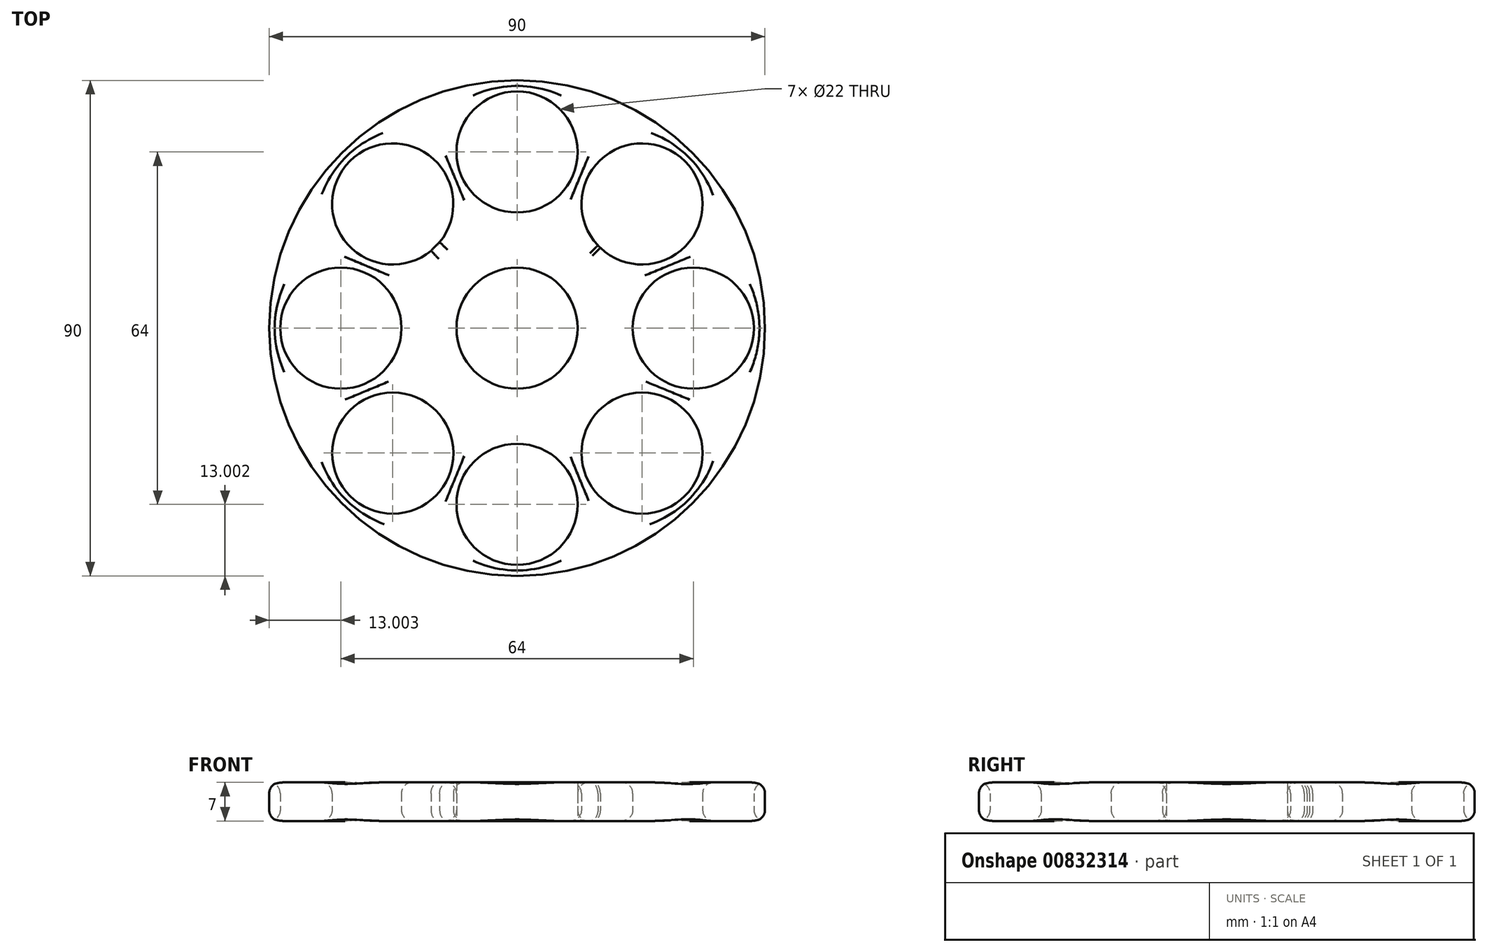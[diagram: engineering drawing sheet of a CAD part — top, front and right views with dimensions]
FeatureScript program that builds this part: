
annotation { "Feature Type Name" : "Feature", "Feature Type Description" : "" }
export const myFeature = defineFeature(function(context is Context, id is Id, definition is map)
    precondition{}
    {
        {
            var Q0;
            Q0=qCreatedBy(makeId("Top.planeOp"),FACE);
            var sketch = newSketch(context, id + "F0", { "sketchPlane" : qUnion([Q0])});
            skCircle(sketch, "E0", {"center": v(-30.12, 6.5) * mm, "radius": 11 * mm});
            skCircle(sketch, "E1", {"center": v(-62.12, 6.5) * mm, "radius": 11 * mm});
            skCircle(sketch, "E2", {"center": v(1.88, 6.5) * mm, "radius": 11 * mm});
            skCircle(sketch, "E3", {"center": v(-30.12, 38.5) * mm, "radius": 11 * mm});
            skCircle(sketch, "E4", {"center": v(-30.12, -25.5) * mm, "radius": 11 * mm});
            skCircle(sketch, "E5", {"center": v(-52.7, -16.2) * mm, "radius": 11 * mm});
            skCircle(sketch, "E6", {"center": v(-7.44, 29.05) * mm, "radius": 11 * mm});
            skCircle(sketch, "E7", {"center": v(-52.7, 29.05) * mm, "radius": 11 * mm});
            skCircle(sketch, "E8", {"center": v(-7.44, -16.2) * mm, "radius": 11 * mm});
            skCircle(sketch, "E9.0", {"center": v(-30.12, 38.5) * mm, "radius": 12 * mm});
            skCircle(sketch, "E10.0", {"center": v(-7.44, 29.05) * mm, "radius": 12 * mm});
            skCircle(sketch, "E11.0", {"center": v(1.88, 6.5) * mm, "radius": 12 * mm});
            skCircle(sketch, "E12.0", {"center": v(-7.44, -16.2) * mm, "radius": 11.13 * mm});
            skCircle(sketch, "E13.0", {"center": v(-7.44, -16.2) * mm, "radius": 12.13 * mm});
            skCircle(sketch, "E14.0", {"center": v(-30.12, -25.5) * mm, "radius": 12 * mm});
            skCircle(sketch, "E15.0", {"center": v(-52.7, -16.2) * mm, "radius": 12 * mm});
            skCircle(sketch, "E16.0", {"center": v(-62.12, 6.5) * mm, "radius": 12 * mm});
            skCircle(sketch, "E17.0", {"center": v(-52.7, 29.05) * mm, "radius": 12 * mm});
            skCircle(sketch, "E18.0", {"center": v(-30.12, 6.5) * mm, "radius": 21 * mm});
            skCircle(sketch, "E19", {"center": v(-30.12, 6.5) * mm, "radius": 45 * mm});
            skSolve(sketch);
        }
        {
            var Q0;
            Q0=makeQuery(id+"F0.imprint","IMPRINT",FACE,{"disambiguationData":[TD([[makeQuery(id+"F0.imprint","IMPRINT",EDGE,{"derivedFrom":sQuery(id+"F0.wireOp",EDGE,"E19")}),1.0]])]});
            var Q1;
            {var subQ0=sQuery(id+"F0.wireOp",EDGE,"E1");Q1=makeQuery(id+"F0.imprint","IMPRINT",FACE,{"disambiguationData":[TD([[makeQuery(id+"F0.imprint","IMPRINT",EDGE,{"derivedFrom":subQ0}),-1.0]])]});}
            var Q2;
            {var subQ0=sQuery(id+"F0.wireOp",EDGE,"E18.0");var subQ1=sQuery(id+"F0.wireOp",EDGE,"E11.0");var subQ2=makeQuery(id+"F0.imprint","INTERSECT",VERTEX,{"disambiguationData":[OD(0.0)],"derivedFrom":[subQ1,subQ0]});Q2=makeQuery(id+"F0.imprint","IMPRINT",FACE,{"disambiguationData":[TD([[makeQuery(id+"F0.imprint","IMPRINT",EDGE,{"disambiguationData":[TD([[subQ2,-1.0]])],"derivedFrom":subQ1}),1.0]])]});}
            var Q3;
            {var subQ0=sQuery(id+"F0.wireOp",EDGE,"E18.0");var subQ1=sQuery(id+"F0.wireOp",EDGE,"E6");var subQ2=makeQuery(id+"F0.imprint","INTERSECT",VERTEX,{"disambiguationData":[OD(0.0)],"derivedFrom":[subQ1,subQ0]});Q3=makeQuery(id+"F0.imprint","IMPRINT",FACE,{"disambiguationData":[TD([[makeQuery(id+"F0.imprint","IMPRINT",EDGE,{"disambiguationData":[TD([[subQ2,-1.0]])],"derivedFrom":subQ1}),-1.0]])]});}
            var Q4;
            {var subQ0=sQuery(id+"F0.wireOp",EDGE,"E2");Q4=makeQuery(id+"F0.imprint","IMPRINT",FACE,{"disambiguationData":[TD([[makeQuery(id+"F0.imprint","IMPRINT",EDGE,{"derivedFrom":subQ0}),-1.0]])]});}
            var Q5;
            {var subQ0=sQuery(id+"F0.wireOp",EDGE,"E18.0");var subQ1=sQuery(id+"F0.wireOp",EDGE,"E7");var subQ2=makeQuery(id+"F0.imprint","INTERSECT",VERTEX,{"disambiguationData":[OD(0.0)],"derivedFrom":[subQ1,subQ0]});Q5=makeQuery(id+"F0.imprint","IMPRINT",FACE,{"disambiguationData":[TD([[makeQuery(id+"F0.imprint","IMPRINT",EDGE,{"disambiguationData":[TD([[subQ2,1.0]])],"derivedFrom":subQ1}),-1.0]])]});}
            var Q6;
            {var subQ0=sQuery(id+"F0.wireOp",EDGE,"E18.0");var subQ1=sQuery(id+"F0.wireOp",EDGE,"E7");var subQ2=makeQuery(id+"F0.imprint","INTERSECT",VERTEX,{"disambiguationData":[OD(0.0)],"derivedFrom":[subQ1,subQ0]});Q6=makeQuery(id+"F0.imprint","IMPRINT",FACE,{"disambiguationData":[TD([[makeQuery(id+"F0.imprint","IMPRINT",EDGE,{"disambiguationData":[TD([[subQ2,-1.0]])],"derivedFrom":subQ1}),-1.0]])]});}
            var Q7;
            {var subQ0=sQuery(id+"F0.wireOp",EDGE,"E18.0");var subQ1=sQuery(id+"F0.wireOp",EDGE,"E12.0");var subQ2=makeQuery(id+"F0.imprint","INTERSECT",VERTEX,{"disambiguationData":[OD(0.0)],"derivedFrom":[subQ1,subQ0]});Q7=makeQuery(id+"F0.imprint","IMPRINT",FACE,{"disambiguationData":[TD([[makeQuery(id+"F0.imprint","IMPRINT",EDGE,{"disambiguationData":[TD([[subQ2,1.0]])],"derivedFrom":subQ1}),-1.0]])]});}
            var Q8;
            {var subQ0=sQuery(id+"F0.wireOp",EDGE,"E18.0");var subQ1=sQuery(id+"F0.wireOp",EDGE,"E9.0");var subQ2=makeQuery(id+"F0.imprint","INTERSECT",VERTEX,{"disambiguationData":[OD(0.0)],"derivedFrom":[subQ1,subQ0]});Q8=makeQuery(id+"F0.imprint","IMPRINT",FACE,{"disambiguationData":[TD([[makeQuery(id+"F0.imprint","IMPRINT",EDGE,{"disambiguationData":[TD([[subQ2,1.0]])],"derivedFrom":subQ1}),1.0]])]});}
            var Q9;
            {var subQ0=sQuery(id+"F0.wireOp",EDGE,"E18.0");var subQ1=sQuery(id+"F0.wireOp",EDGE,"E12.0");var subQ2=makeQuery(id+"F0.imprint","INTERSECT",VERTEX,{"disambiguationData":[OD(0.0)],"derivedFrom":[subQ1,subQ0]});Q9=makeQuery(id+"F0.imprint","IMPRINT",FACE,{"disambiguationData":[TD([[makeQuery(id+"F0.imprint","IMPRINT",EDGE,{"disambiguationData":[TD([[subQ2,-1.0]])],"derivedFrom":subQ1}),-1.0]])]});}
            var Q10;
            {var subQ0=sQuery(id+"F0.wireOp",EDGE,"E18.0");var subQ1=sQuery(id+"F0.wireOp",EDGE,"E16.0");var subQ2=makeQuery(id+"F0.imprint","INTERSECT",VERTEX,{"disambiguationData":[OD(0.0)],"derivedFrom":[subQ1,subQ0]});Q10=makeQuery(id+"F0.imprint","IMPRINT",FACE,{"disambiguationData":[TD([[makeQuery(id+"F0.imprint","IMPRINT",EDGE,{"disambiguationData":[TD([[subQ2,1.0]])],"derivedFrom":subQ1}),1.0]])]});}
            var Q11;
            {var subQ0=sQuery(id+"F0.wireOp",EDGE,"E18.0");var subQ1=sQuery(id+"F0.wireOp",EDGE,"E14.0");var subQ2=makeQuery(id+"F0.imprint","INTERSECT",VERTEX,{"disambiguationData":[OD(0.0)],"derivedFrom":[subQ1,subQ0]});Q11=makeQuery(id+"F0.imprint","IMPRINT",FACE,{"disambiguationData":[TD([[makeQuery(id+"F0.imprint","IMPRINT",EDGE,{"disambiguationData":[TD([[subQ2,1.0]])],"derivedFrom":subQ1}),1.0]])]});}
            var Q12;
            Q12=makeQuery(id+"F0.imprint","IMPRINT",FACE,{"disambiguationData":[TD([[makeQuery(id+"F0.imprint","IMPRINT",EDGE,{"derivedFrom":sQuery(id+"F0.wireOp",EDGE,"E5")}),-1.0]])]});
            var Q13;
            {var subQ0=sQuery(id+"F0.wireOp",EDGE,"E18.0");var subQ1=sQuery(id+"F0.wireOp",EDGE,"E15.0");var subQ2=makeQuery(id+"F0.imprint","INTERSECT",VERTEX,{"disambiguationData":[OD(0.0)],"derivedFrom":[subQ1,subQ0]});Q13=makeQuery(id+"F0.imprint","IMPRINT",FACE,{"disambiguationData":[TD([[makeQuery(id+"F0.imprint","IMPRINT",EDGE,{"disambiguationData":[TD([[subQ2,1.0]])],"derivedFrom":subQ1}),1.0]])]});}
            var Q14;
            {var subQ0=sQuery(id+"F0.wireOp",EDGE,"E18.0");var subQ1=sQuery(id+"F0.wireOp",EDGE,"E6");var subQ2=makeQuery(id+"F0.imprint","INTERSECT",VERTEX,{"disambiguationData":[OD(0.0)],"derivedFrom":[subQ1,subQ0]});Q14=makeQuery(id+"F0.imprint","IMPRINT",FACE,{"disambiguationData":[TD([[makeQuery(id+"F0.imprint","IMPRINT",EDGE,{"disambiguationData":[TD([[subQ2,1.0]])],"derivedFrom":subQ1}),-1.0]])]});}
            var Q15;
            Q15=makeQuery(id+"F0.imprint","IMPRINT",FACE,{"disambiguationData":[TD([[makeQuery(id+"F0.imprint","IMPRINT",EDGE,{"derivedFrom":sQuery(id+"F0.wireOp",EDGE,"E8")}),-1.0]])]});
            var Q16;
            {var subQ0=sQuery(id+"F0.wireOp",EDGE,"E18.0");var subQ1=sQuery(id+"F0.wireOp",EDGE,"E12.0");var subQ2=makeQuery(id+"F0.imprint","INTERSECT",VERTEX,{"disambiguationData":[OD(0.0)],"derivedFrom":[subQ1,subQ0]});Q16=makeQuery(id+"F0.imprint","IMPRINT",FACE,{"disambiguationData":[TD([[makeQuery(id+"F0.imprint","IMPRINT",EDGE,{"disambiguationData":[TD([[subQ2,1.0]])],"derivedFrom":subQ1}),1.0]])]});}
            var Q17;
            {var subQ0=sQuery(id+"F0.wireOp",EDGE,"E18.0");var subQ1=sQuery(id+"F0.wireOp",EDGE,"E7");var subQ2=makeQuery(id+"F0.imprint","INTERSECT",VERTEX,{"disambiguationData":[OD(0.0)],"derivedFrom":[subQ1,subQ0]});Q17=makeQuery(id+"F0.imprint","IMPRINT",FACE,{"disambiguationData":[TD([[makeQuery(id+"F0.imprint","IMPRINT",EDGE,{"disambiguationData":[TD([[subQ2,1.0]])],"derivedFrom":subQ1}),1.0]])]});}
            var Q18;
            {var subQ0=sQuery(id+"F0.wireOp",EDGE,"E18.0");var subQ1=sQuery(id+"F0.wireOp",EDGE,"E6");var subQ2=makeQuery(id+"F0.imprint","INTERSECT",VERTEX,{"disambiguationData":[OD(0.0)],"derivedFrom":[subQ1,subQ0]});Q18=makeQuery(id+"F0.imprint","IMPRINT",FACE,{"disambiguationData":[TD([[makeQuery(id+"F0.imprint","IMPRINT",EDGE,{"disambiguationData":[TD([[subQ2,1.0]])],"derivedFrom":subQ1}),1.0]])]});}
            var Q19;
            Q19=makeQuery(id+"F0.imprint","IMPRINT",FACE,{"disambiguationData":[TD([[makeQuery(id+"F0.imprint","IMPRINT",EDGE,{"derivedFrom":sQuery(id+"F0.wireOp",EDGE,"E0")}),-1.0]])]});
            var Q20;
            {var subQ0=sQuery(id+"F0.wireOp",EDGE,"E3");Q20=makeQuery(id+"F0.imprint","IMPRINT",FACE,{"disambiguationData":[TD([[makeQuery(id+"F0.imprint","IMPRINT",EDGE,{"derivedFrom":subQ0}),-1.0]])]});}
            var Q21;
            {var subQ0=sQuery(id+"F0.wireOp",EDGE,"E4");Q21=makeQuery(id+"F0.imprint","IMPRINT",FACE,{"disambiguationData":[TD([[makeQuery(id+"F0.imprint","IMPRINT",EDGE,{"derivedFrom":subQ0}),-1.0]])]});}
            extrude(context, id + "F1", {"entities" : qUnion([Q0, Q1, Q2, Q3, Q4, Q5, Q6, Q7, Q8, Q9, Q10, Q11, Q12, Q13, Q14, Q15, Q16, Q17, Q18, Q19, Q20, Q21]), "depth" : 7 * mm, "offsetDistance" : 25 * mm});
        }
        {
            var Q0;
            Q0=makeQuery(id+"F1.opExtrude","CAP_EDGE",EDGE,{"disambiguationData":[OSD([sQuery(id+"F0.wireOp",EDGE,"E19")])],"isStart":false});
            var Q1;
            Q1=makeQuery(id+"F1.opExtrude","CAP_EDGE",EDGE,{"disambiguationData":[OSD([sQuery(id+"F0.wireOp",EDGE,"E19")])],"isStart":true});
            var Q2;
            Q2=makeQuery(id+"F1.opExtrude","CAP_EDGE",EDGE,{"disambiguationData":[OSD([sQuery(id+"F0.wireOp",EDGE,"E1")])],"isStart":false});
            var Q3;
            Q3=makeQuery(id+"F1.opExtrude","CAP_EDGE",EDGE,{"disambiguationData":[OSD([sQuery(id+"F0.wireOp",EDGE,"E5")])],"isStart":false});
            var Q4;
            Q4=makeQuery(id+"F1.opExtrude","CAP_EDGE",EDGE,{"disambiguationData":[OSD([sQuery(id+"F0.wireOp",EDGE,"E7")])],"isStart":false});
            var Q5;
            {var subQ0=sQuery(id+"F0.wireOp",EDGE,"E18.0");var subQ1=sQuery(id+"F0.wireOp",EDGE,"E7");Q5=makeQuery(id+"F1.opExtrude","CAP_EDGE",EDGE,{"disambiguationData":[OSD([subQ0]),TDD([makeQuery(id+"F0.imprint","IMPRINT",EDGE,{"disambiguationData":[TD([[makeQuery(id+"F0.imprint","INTERSECT",VERTEX,{"disambiguationData":[OD(0.0)],"derivedFrom":[subQ1,subQ0]}),-1.0]])],"derivedFrom":subQ0})])],"isStart":false});}
            var Q6;
            Q6=makeQuery(id+"F1.opExtrude","CAP_EDGE",EDGE,{"disambiguationData":[OSD([sQuery(id+"F0.wireOp",EDGE,"E3")])],"isStart":false});
            var Q7;
            Q7=makeQuery(id+"F1.opExtrude","CAP_EDGE",EDGE,{"disambiguationData":[OSD([sQuery(id+"F0.wireOp",EDGE,"E6")])],"isStart":false});
            var Q8;
            {var subQ0=sQuery(id+"F0.wireOp",EDGE,"E18.0");var subQ1=sQuery(id+"F0.wireOp",EDGE,"E6");Q8=makeQuery(id+"F1.opExtrude","CAP_EDGE",EDGE,{"disambiguationData":[OSD([subQ0]),TDD([makeQuery(id+"F0.imprint","IMPRINT",EDGE,{"disambiguationData":[TD([[makeQuery(id+"F0.imprint","INTERSECT",VERTEX,{"disambiguationData":[OD(0.0)],"derivedFrom":[subQ1,subQ0]}),-1.0]])],"derivedFrom":subQ0})])],"isStart":false});}
            var Q9;
            Q9=makeQuery(id+"F1.opExtrude","CAP_EDGE",EDGE,{"disambiguationData":[OSD([sQuery(id+"F0.wireOp",EDGE,"E2")])],"isStart":false});
            var Q10;
            Q10=makeQuery(id+"F1.opExtrude","CAP_EDGE",EDGE,{"disambiguationData":[OSD([sQuery(id+"F0.wireOp",EDGE,"E8")])],"isStart":false});
            var Q11;
            Q11=makeQuery(id+"F1.opExtrude","CAP_EDGE",EDGE,{"disambiguationData":[OSD([sQuery(id+"F0.wireOp",EDGE,"E4")])],"isStart":false});
            var Q12;
            Q12=makeQuery(id+"F1.opExtrude","CAP_EDGE",EDGE,{"disambiguationData":[OSD([sQuery(id+"F0.wireOp",EDGE,"E4")])],"isStart":true});
            var Q13;
            Q13=makeQuery(id+"F1.opExtrude","CAP_EDGE",EDGE,{"disambiguationData":[OSD([sQuery(id+"F0.wireOp",EDGE,"E8")])],"isStart":true});
            var Q14;
            Q14=makeQuery(id+"F1.opExtrude","CAP_EDGE",EDGE,{"disambiguationData":[OSD([sQuery(id+"F0.wireOp",EDGE,"E2")])],"isStart":true});
            var Q15;
            Q15=makeQuery(id+"F1.opExtrude","CAP_EDGE",EDGE,{"disambiguationData":[OSD([sQuery(id+"F0.wireOp",EDGE,"E6")])],"isStart":true});
            var Q16;
            {var subQ0=sQuery(id+"F0.wireOp",EDGE,"E18.0");var subQ1=sQuery(id+"F0.wireOp",EDGE,"E6");Q16=makeQuery(id+"F1.opExtrude","CAP_EDGE",EDGE,{"disambiguationData":[OSD([subQ0]),TDD([makeQuery(id+"F0.imprint","IMPRINT",EDGE,{"disambiguationData":[TD([[makeQuery(id+"F0.imprint","INTERSECT",VERTEX,{"disambiguationData":[OD(0.0)],"derivedFrom":[subQ1,subQ0]}),-1.0]])],"derivedFrom":subQ0})])],"isStart":true});}
            var Q17;
            Q17=makeQuery(id+"F1.opExtrude","CAP_EDGE",EDGE,{"disambiguationData":[OSD([sQuery(id+"F0.wireOp",EDGE,"E3")])],"isStart":true});
            var Q18;
            Q18=makeQuery(id+"F1.opExtrude","CAP_EDGE",EDGE,{"disambiguationData":[OSD([sQuery(id+"F0.wireOp",EDGE,"E5")])],"isStart":true});
            var Q19;
            Q19=makeQuery(id+"F1.opExtrude","CAP_EDGE",EDGE,{"disambiguationData":[OSD([sQuery(id+"F0.wireOp",EDGE,"E1")])],"isStart":true});
            var Q20;
            Q20=makeQuery(id+"F1.opExtrude","CAP_EDGE",EDGE,{"disambiguationData":[OSD([sQuery(id+"F0.wireOp",EDGE,"E7")])],"isStart":true});
            var Q21;
            {var subQ0=sQuery(id+"F0.wireOp",EDGE,"E18.0");var subQ1=sQuery(id+"F0.wireOp",EDGE,"E7");Q21=makeQuery(id+"F1.opExtrude","CAP_EDGE",EDGE,{"disambiguationData":[OSD([subQ0]),TDD([makeQuery(id+"F0.imprint","IMPRINT",EDGE,{"disambiguationData":[TD([[makeQuery(id+"F0.imprint","INTERSECT",VERTEX,{"disambiguationData":[OD(0.0)],"derivedFrom":[subQ1,subQ0]}),-1.0]])],"derivedFrom":subQ0})])],"isStart":true});}
            fillet(context, id + "F2", {"entities" : qUnion([Q0, Q1, Q2, Q3, Q4, Q5, Q6, Q7, Q8, Q9, Q10, Q11, Q12, Q13, Q14, Q15, Q16, Q17, Q18, Q19, Q20, Q21]), "radius" : 2 * mm, "tangentPropagation" : true, "allowEdgeOverflow" : false});
        }
    });
